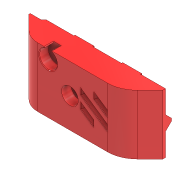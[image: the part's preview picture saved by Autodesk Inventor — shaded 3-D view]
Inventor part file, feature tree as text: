
AUTODESK INVENTOR PART (.ipt)
format: ipt  version: 2021 (Build 250183000, 183)  size: 371,712 bytes
history: native  units: mm
features: reference x11, other x10, sketch x8, extrude x7, chamfer x4, fillet x3, projected_geometry x2, plane x1, direct_edit x1, hole x1, delete_face x1, move_body x1
ambient origin geometry x8: Origin, YZ Plane, XZ Plane, XY Plane, X Axis, Y Axis, Z Axis, Center Point
bodies: Volumenkörper1 (feature_tree)
feature tree (50):
  extrude  "Extrusion1"  Depth=6.4mm
  plane  "Arbeitsebene1"
  extrude  "Extrusion2"  Depth=6.4mm
  chamfer  "Fase1"  Distance=6.4mm
  extrude  "Extrusion3"  Depth=0.2mm
  direct_edit  "Direktbearbeitung1"
  fillet  "Rundung1"  Radius=5.0mm
  extrude  "Extrusion4"  Depth=0.2mm
  hole  "Bohrung1"  [1 undecoded]
  chamfer  "Fase3"  Distance=0.1mm
  extrude  "Extrusion5"  Depth=0.2mm TaperAngle=0.0deg
  chamfer  "Fase4"  Distance=7.0mm Angle=45.0deg
  delete_face  "Fläche löschen1"
  extrude  "Extrusion7"  TaperAngle=45.0deg  [1 undecoded]
  fillet  "Rundung4"  Radius=0.05mm
  extrude  "Extrusion8"  TaperAngle=45.0deg  [1 undecoded]
  chamfer  "Fase5"  Distance=0.05mm
  fillet  "Rundung5"  Radius=0.4mm
  sketch  "Skizze1"  dims[d0=3.25mm d1=6.4mm]
  reference  "Referenz1"
  sketch  "Skizze2"  dims[d2=6.4mm d3=6.4mm]
  reference  "Referenz2"
  sketch  "Skizze3"  dims[d4=6.4mm]
  reference  "Referenz3"
  reference  "Referenz4"
  reference  "Referenz5"
  sketch  "Skizze4"  dims[d5=6.4mm]
  projected_geometry  "Projizierte Kontur1"
  sketch  "Skizze5"  dims[d6=5.0mm]
  projected_geometry  "Projizierte Kontur2"
  sketch  "Skizze6"  dims[d7=5.0mm]
  reference  "Referenz6"
  reference  "Referenz7"
  reference  "Referenz8"
  reference  "Referenz9"
  reference  "Referenz10"
  sketch  "Skizze8"  dims[d8=6.4mm]
  reference  "Referenz13"
  sketch  "Skizze9"  dims[d9=6.4mm d10=6.4mm d11=5.0mm d12=5.0mm d13=0.1mm d14=0.4mm d15=0.0mm d16=0.1mm d17=7.9mm d18=0.0mm d19=7.0mm d20=2.0mm d21=45.0deg d22=45.0deg d23=0.05mm d24=45.0deg d25=0.05mm d26=0.4mm d27=8.0mm d28=0.0mm d29=0.0mm d30=0.0mm d31=0.2mm d32=10.0mm d97=25.438174mm d99=2.2mm d102=1.913043mm d103=5.5mm d104=11.0mm d106=0.0mm d110=2.2mm d111=11.0mm d113=2.2mm d114=5.5mm d118=0.0mm d119=1.913043mm d124=9.092487mm d125=10.426087mm d126=25.215728mm d127=20.0mm d128=0.0mm d129=4.786957mm d130=1.0mm d131=0.0mm d135=25.215728mm d136=20.0mm d137=12.607864mm d138=10.0mm d139=3.2mm d140=6.0mm d141=5.6mm d142=3.2mm d143=90.0deg d144=8.0mm d145=20.594885mm d146=20.0mm d147=10.0mm d148=12.607864mm d149=5.6mm d150=0.8mm d151=2.0mm d152=45.0deg d153=6.0mm d154=7.397555mm d155=3.698777mm d156=3.1mm d157=3.1mm d158=0.0mm d159=2.0mm d160=0.2mm d161=2.0mm d162=45.0deg d167=0.0mm d168=0.4mm d169=0.0mm d170=0.0mm d171=7.0mm d172=0.01mm d173=0.05mm d175=0.05mm d176=4.95mm d177=0.0mm d178=1.99mm d179=2.0mm d180=45.0deg d181=0.2mm]
  other  "<userpath>\Desktop\Voron-2-2.4r1\Custom\Misumi GE5C\Gruppe.iam"
  other  "Gruppe.iam"
  other  "Z-Joint-Normal:1"
  move_body  "Verschieben1"
  other  "X Axis:1"
  other  "XY Joint - Right:1"
  other  "Microswitch Endstop Pod:1"
  other  "Bauteil538"
  other  "Bauteil608"
  other  "Hall Effect Endstop Pod:1"
  other  "Bauteil546"
note: 3 required parameter values undecoded (feature->parameter linkage not recoverable at this tier; creation-order binding heuristic only, values carry confidence <= 0.55)
